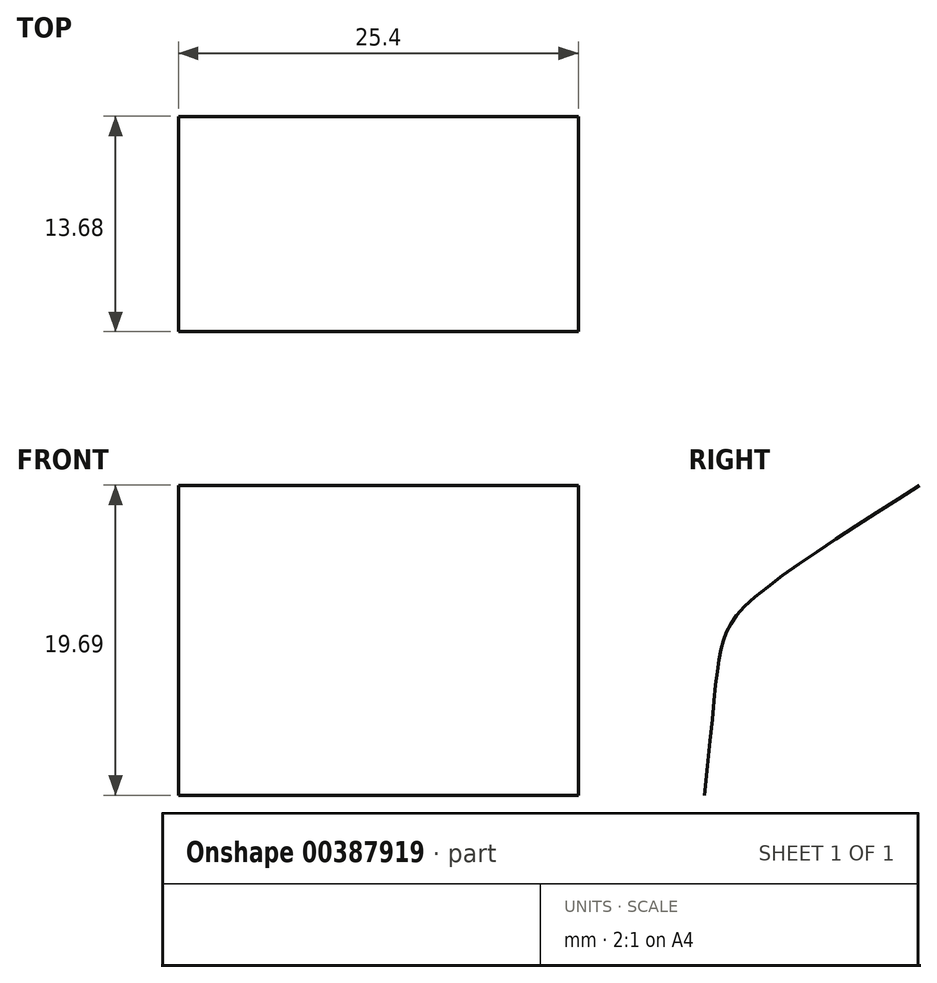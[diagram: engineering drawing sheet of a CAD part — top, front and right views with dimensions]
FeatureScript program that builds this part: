
annotation { "Feature Type Name" : "Feature", "Feature Type Description" : "" }
export const myFeature = defineFeature(function(context is Context, id is Id, definition is map)
    precondition{}
    {
        {
            var Q0;
            Q0=qCreatedBy(makeId("Right.planeOp"),FACE);
            var sketch = newSketch(context, id + "F0", { "sketchPlane" : qUnion([Q0])});
            skFitSpline(sketch, "E0", {"points": [v(-27.23, -4.08) * mm, v(-26.12, 5.4) * mm, v(-24.66, 7.9) * mm, v(-13.55, 15.6) * mm], "startDerivative": vector(5.14, 45.52) * mm, "endDerivative": vector(31.4, 20.16) * mm});
            skSolve(sketch);
        }
        {
            var Q0;
            Q0=sQuery(id+"F0.wireOp",EDGE,"E0");
            extrude(context, id + "F1", {"bodyType" : ToolBodyType.SURFACE, "surfaceEntities" : qUnion([Q0]), "depth" : 25.4 * mm});
        }
    });
